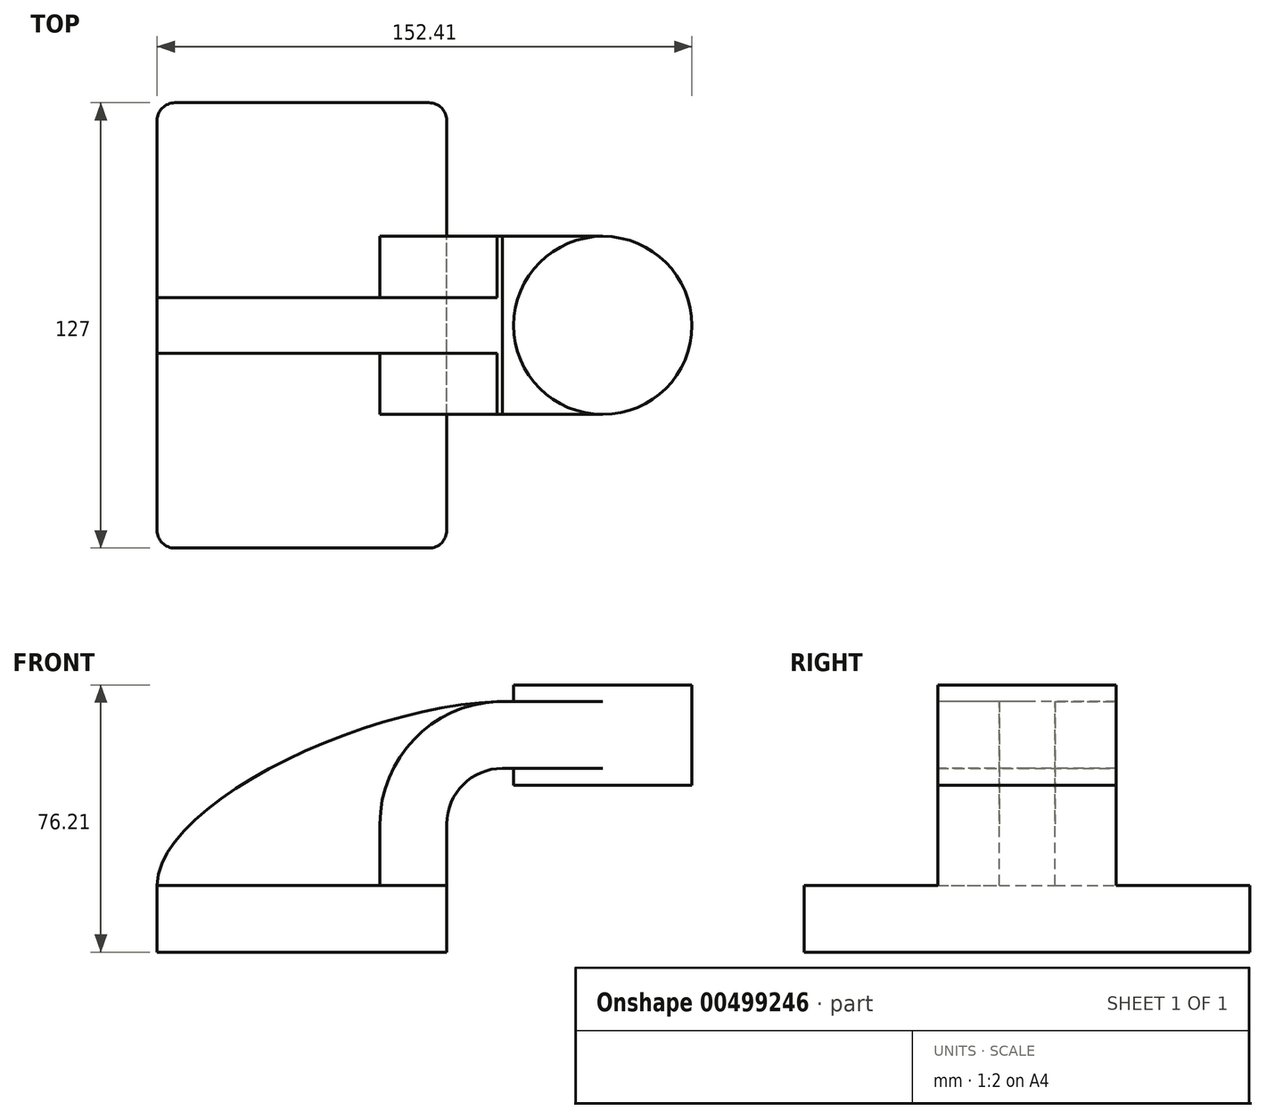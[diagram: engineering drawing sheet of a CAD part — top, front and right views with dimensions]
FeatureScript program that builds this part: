
annotation { "Feature Type Name" : "Feature", "Feature Type Description" : "" }
export const myFeature = defineFeature(function(context is Context, id is Id, definition is map)
    precondition{}
    {
        {
            var Q0;
            Q0=qCreatedBy(makeId("Front.planeOp"),FACE);
            var sketch = newSketch(context, id + "F0", { "sketchPlane" : qUnion([Q0])});
            skLineSegment(sketch, "E0.bottom", {"start": v(-41.28, -9.53) * mm, "end": v(41.28, -9.53) * mm});
            skLineSegment(sketch, "E0.top", {"start": v(-41.28, 9.53) * mm, "end": v(41.28, 9.53) * mm});
            skLineSegment(sketch, "E0.left", {"start": v(-41.28, -9.53) * mm, "end": v(-41.28, 9.53) * mm});
            skLineSegment(sketch, "E0.right", {"start": v(41.28, -9.53) * mm, "end": v(41.28, 9.53) * mm});
            skPoint(sketch, "E0.middle", {"position": v(0, 0) * mm});
            skLineSegment(sketch, "E1.bottom", {"start": v(60.33, 38.1) * mm, "end": v(111.13, 38.1) * mm});
            skLineSegment(sketch, "E1.top", {"start": v(60.33, 66.68) * mm, "end": v(111.13, 66.68) * mm});
            skLineSegment(sketch, "E1.left", {"start": v(60.33, 38.1) * mm, "end": v(60.32, 66.67) * mm});
            skLineSegment(sketch, "E1.right", {"start": v(111.13, 38.1) * mm, "end": v(111.13, 66.67) * mm});
            skPoint(sketch, "E1.middle", {"position": v(85.73, 52.39) * mm});
            skLineSegment(sketch, "E2", {"start": v(41.27, 9.53) * mm, "end": v(41.27, 27) * mm});
            skArc(sketch, "E3", {"start": v(41.27, 27) * mm, "mid": v(45.92, 38.23) * mm, "end": v(57.15, 42.88) * mm});
            skLineSegment(sketch, "E4", {"start": v(57.15, 42.88) * mm, "end": v(85.73, 42.88) * mm});
            skLineSegment(sketch, "E5.0", {"start": v(57.15, 61.93) * mm, "end": v(85.73, 61.93) * mm});
            skArc(sketch, "E5.1", {"start": v(22.22, 27) * mm, "mid": v(32.45, 51.7) * mm, "end": v(57.15, 61.93) * mm});
            skLineSegment(sketch, "E5.2", {"start": v(22.22, 9.53) * mm, "end": v(22.22, 27) * mm});
            skLineSegment(sketch, "E6", {"start": v(85.73, 38.1) * mm, "end": v(85.73, 66.68) * mm});
            skFitSpline(sketch, "E7", {"points": [v(-41.28, 9.53) * mm, v(57.15, 61.93) * mm], "startDerivative": vector(1.17, 70.94) * mm, "endDerivative": vector(113.6, 1.41) * mm});
            skSolve(sketch);
        }
        {
            var Q0;
            Q0=makeQuery(id+"F0.imprint","IMPRINT",FACE,{"disambiguationData":[TD([[makeQuery(id+"F0.imprint","IMPRINT",EDGE,{"derivedFrom":sQuery(id+"F0.wireOp",EDGE,"E0.bottom")}),1.0]])]});
            extrude(context, id + "F1", {"entities" : qUnion([Q0]), "endBound" : BoundingType.SYMMETRIC, "depth" : 127 * mm});
        }
        {
            var Q0;
            {var subQ0=sQuery(id+"F0.wireOp",EDGE,"E4");var subQ1=sQuery(id+"F0.wireOp",EDGE,"E1.left");var subQ2=makeQuery(id+"F0.imprint","INTERSECT",VERTEX,{"derivedFrom":[subQ1,subQ0]});Q0=makeQuery(id+"F0.imprint","IMPRINT",FACE,{"disambiguationData":[TD([[makeQuery(id+"F0.imprint","IMPRINT",EDGE,{"disambiguationData":[TD([[subQ2,-1.0]])],"derivedFrom":subQ1}),-1.0]])]});}
            var Q1;
            {var subQ1=sQuery(id+"F0.wireOp",EDGE,"E2");Q1=makeQuery(id+"F0.imprint","IMPRINT",FACE,{"disambiguationData":[TD([[makeQuery(id+"F0.imprint","IMPRINT",EDGE,{"derivedFrom":subQ1}),1.0]])]});}
            extrude(context, id + "F2", {"entities" : qUnion([Q0, Q1]), "operationType" : NewBodyOperationType.ADD, "endBound" : BoundingType.SYMMETRIC, "depth" : 50.8 * mm});
        }
        {
            var Q0;
            {var subQ3=sQuery(id+"F0.wireOp",EDGE,"E5.2");Q0=makeQuery(id+"F0.imprint","IMPRINT",FACE,{"disambiguationData":[TD([[makeQuery(id+"F0.imprint","IMPRINT",EDGE,{"derivedFrom":subQ3}),1.0]])]});}
            extrude(context, id + "F3", {"entities" : qUnion([Q0]), "operationType" : NewBodyOperationType.ADD, "endBound" : BoundingType.SYMMETRIC, "depth" : 15.88 * mm});
        }
        {
            var Q0;
            {var subQ4=sQuery(id+"F0.wireOp",EDGE,"E1.right");Q0=makeQuery(id+"F0.imprint","IMPRINT",FACE,{"disambiguationData":[TD([[makeQuery(id+"F0.imprint","IMPRINT",EDGE,{"derivedFrom":subQ4}),1.0]])]});}
            var Q1;
            Q1=sQuery(id+"F0.wireOp",EDGE,"E6");
            revolve(context, id + "F4", {"operationType" : NewBodyOperationType.ADD, "entities" : qUnion([Q0]), "axis" : qUnion([Q1]), "revolveType" : RevolveType.FULL});
        }
        {
            var Q0;
            Q0=makeQuery(id+"F1.opExtrude","CAP_EDGE",EDGE,{"disambiguationData":[OSD([sQuery(id+"F0.wireOp",EDGE,"E0.right")])],"isStart":false});
            var Q1;
            Q1=makeQuery(id+"F1.opExtrude","CAP_EDGE",EDGE,{"disambiguationData":[OSD([sQuery(id+"F0.wireOp",EDGE,"E0.left")])],"isStart":false});
            var Q2;
            Q2=makeQuery(id+"F1.opExtrude","CAP_EDGE",EDGE,{"disambiguationData":[OSD([sQuery(id+"F0.wireOp",EDGE,"E0.left")])],"isStart":true});
            var Q3;
            Q3=makeQuery(id+"F1.opExtrude","CAP_EDGE",EDGE,{"disambiguationData":[OSD([sQuery(id+"F0.wireOp",EDGE,"E0.right")])],"isStart":true});
            fillet(context, id + "F5", {"entities" : qUnion([Q0, Q1, Q2, Q3]), "radius" : 5.08 * mm, "tangentPropagation" : true, "allowEdgeOverflow" : false});
        }
    });
